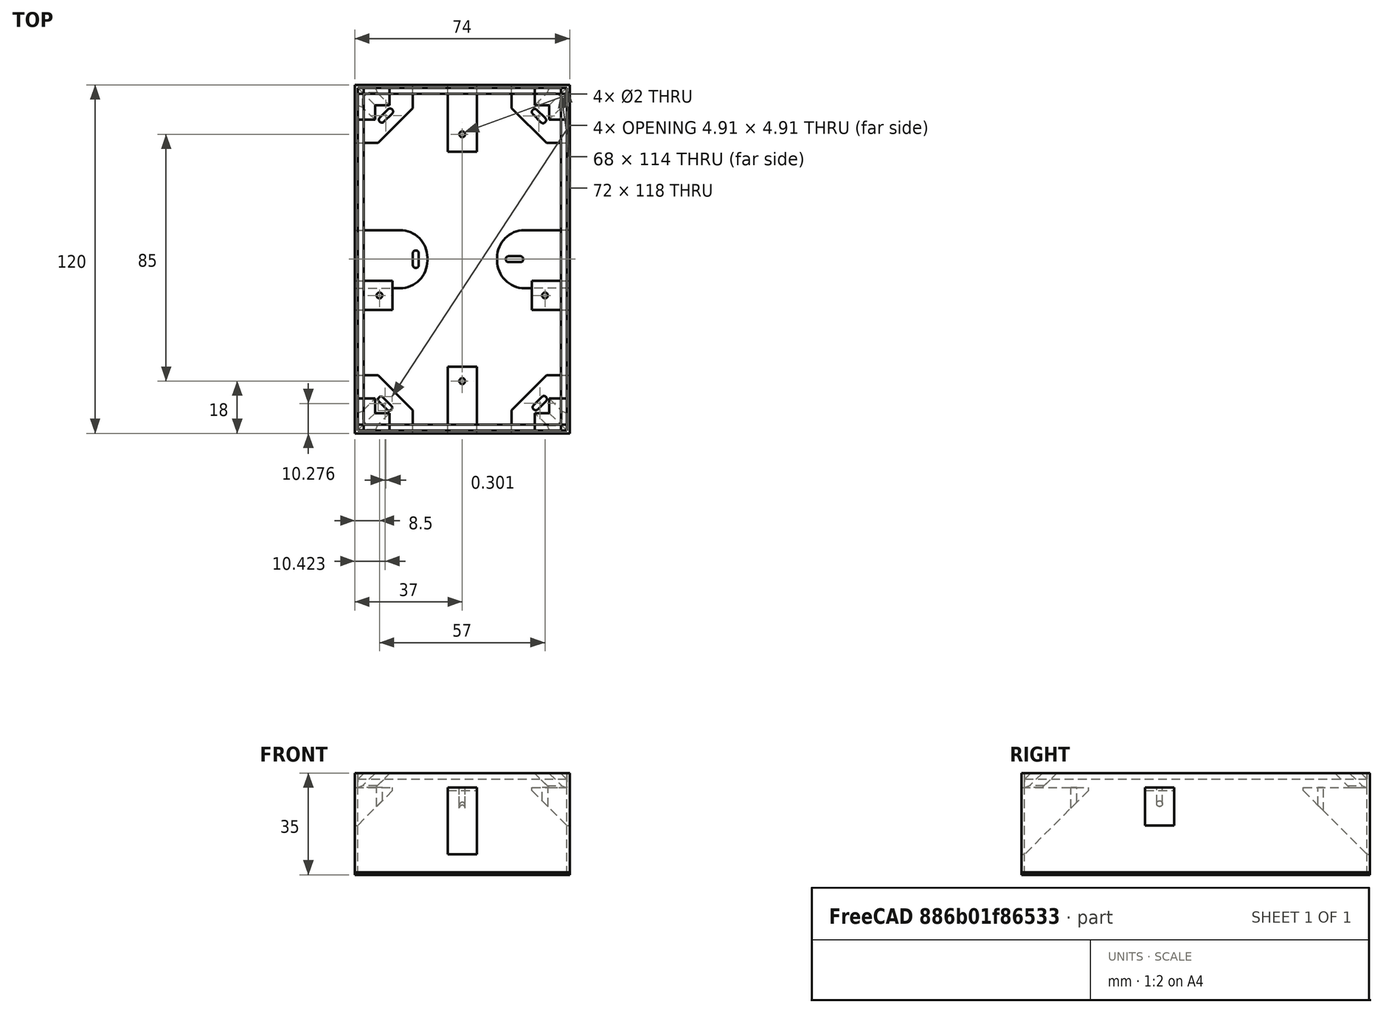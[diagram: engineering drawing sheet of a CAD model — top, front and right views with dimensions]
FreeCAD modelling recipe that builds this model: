
FCSTD DOCUMENT  (FreeCAD 0.16R)
Label: sonoff-T1-US-aufputz-v2-3
License: All rights reserved
LicenseURL: http://en.wikipedia.org/wiki/All_rights_reserved
objects: Part::Box×32, Part::Chamfer×20, Part::Cut×16, Part::Fillet×8, Part::Cylinder×4
note: 80 computed .brp shape members not serialized (recipe doc carries the construction recipe); baked Part::Feature solids carry a one-line shape summary decoded from their .brp

FEATURE [Part::Box] Box  label="Basis"
  Height = 35
  Length = 74
  Width = 120
FEATURE [Part::Box] Box001  label="Ausschnitt"
  Height = 35
  Length = 72
  Placement = pos=(1,1,0) rot=(0,0,1;0rad)
  Width = 118
FEATURE [Part::Cut] Cut
  Base = -> Box
  Tool = -> Box001
FEATURE [Part::Box] Box016  label="Cube012"
  Height = 0.8
  Length = 20
  Width = 20
FEATURE [Part::Box] Box017  label="Cube013"
  Height = 0.8
  Length = 20
  Placement = pos=(54,0,0) rot=(0,0,1;0rad)
  Width = 20
FEATURE [Part::Box] Box018  label="Cube014"
  Height = 0.8
  Length = 20
  Placement = pos=(54,100,0) rot=(0,0,1;0rad)
  Width = 20
FEATURE [Part::Box] Box019  label="Cube015"
  Height = 0.8
  Length = 20
  Placement = pos=(0,100,0) rot=(0,0,1;0rad)
  Width = 20
FEATURE [Part::Box] Box015  label="Basis002"
  Height = 0.8
  Length = 68
  Placement = pos=(3,3,0) rot=(0,0,1;0rad)
  Width = 114
FEATURE [Part::Box] Box014  label="Basis001"
  Height = 0.8
  Length = 74
  Width = 120
FEATURE [Part::Cut] Cut009
  Base = -> Box014
  Tool = -> Box015
FEATURE [Part::Chamfer] Chamfer
  Base = -> Box019
  Edges = 1 edges r=12: [Edge5]
FEATURE [Part::Chamfer] Chamfer001
  Base = -> Box018
  Edges = 1 edges r=12: [Edge1]
FEATURE [Part::Chamfer] Chamfer002
  Base = -> Box017
  Edges = 1 edges r=12: [Edge3]
FEATURE [Part::Chamfer] Chamfer003
  Base = -> Box016
  Edges = 1 edges r=12: [Edge7]
FEATURE [Part::Box] Box024  label="Cube019"
  Height = 5
  Length = 5
  Placement = pos=(63,109,30) rot=(0,0,1;0rad)
  Width = 5
FEATURE [Part::Box] Box025  label="Cube020"
  Height = 5
  Length = 11
  Placement = pos=(63,109,30) rot=(0,0,1;0rad)
  Width = 11
FEATURE [Part::Cut] Cut012
  Base = -> Box025
  Tool = -> Box024
FEATURE [Part::Chamfer] Chamfer004
  Base = -> Cut012
  Edges = 4 edges r=4.9: [Edge4,Edge5,Edge15,Edge16]
  Placement = pos=(-1,-1,0) rot=(0,0,1;0rad)
FEATURE [Part::Box] Box028  label="Cube023"
  Height = 2
  Length = 72
  Placement = pos=(1,1,33) rot=(0,0,1;0rad)
  Width = 2
FEATURE [Part::Box] Box029  label="Cube024"
  Height = 2
  Length = 2
  Placement = pos=(1,1,33) rot=(0,0,1;0rad)
  Width = 118
FEATURE [Part::Box] Box030  label="Cube025"
  Height = 2
  Length = 72
  Placement = pos=(1,117,33) rot=(0,0,1;0rad)
  Width = 2
FEATURE [Part::Box] Box031  label="Cube026"
  Height = 2
  Length = 2
  Placement = pos=(71,1,33) rot=(0,0,1;0rad)
  Width = 118
FEATURE [Part::Chamfer] Chamfer008
  Base = -> Box031
  Edges = 1 edges r=1.9: [Edge4]
FEATURE [Part::Chamfer] Chamfer009
  Base = -> Box030
  Edges = 1 edges r=1.9: [Edge9]
FEATURE [Part::Chamfer] Chamfer010
  Base = -> Box029
  Edges = 1 edges r=1.9: [Edge8]
FEATURE [Part::Chamfer] Chamfer011
  Base = -> Box028
  Edges = 1 edges r=1.9: [Edge11]
FEATURE [Part::Box] Box032  label="Cube027"
  Height = 5
  Length = 11
  Placement = pos=(63,109,30) rot=(0,0,1;0rad)
  Width = 11
FEATURE [Part::Box] Box033  label="Cube028"
  Height = 5
  Length = 5
  Placement = pos=(63,109,30) rot=(0,0,1;0rad)
  Width = 5
FEATURE [Part::Cut] Cut013
  Base = -> Box032
  Tool = -> Box033
FEATURE [Part::Chamfer] Chamfer012
  Base = -> Cut013
  Edges = 4 edges r=4.9: [Edge4,Edge5,Edge15,Edge16]
  Placement = pos=(121,45,0) rot=(0,0,1;1.5708rad)
FEATURE [Part::Chamfer] Chamfer013
  Base = -> Chamfer004
  Edges = 2 edges r=0.9: [Edge19,Edge23]
FEATURE [Part::Chamfer] Chamfer014
  Base = -> Chamfer012
  Edges = 2 edges r=0.9: [Edge19,Edge23]
FEATURE [Part::Box] Box034  label="Cube029"
  Height = 5
  Length = 5
  Placement = pos=(63,109,30) rot=(0,0,1;0rad)
  Width = 5
FEATURE [Part::Box] Box035  label="Cube030"
  Height = 5
  Length = 11
  Placement = pos=(63,109,30) rot=(0,0,1;0rad)
  Width = 11
FEATURE [Part::Cut] Cut014
  Base = -> Box035
  Tool = -> Box034
FEATURE [Part::Chamfer] Chamfer015
  Base = -> Cut014
  Edges = 4 edges r=4.9: [Edge4,Edge5,Edge15,Edge16]
  Placement = pos=(-1,-1,0) rot=(0,0,1;0rad)
FEATURE [Part::Chamfer] Chamfer016
  Base = -> Chamfer015
  Edges = 2 edges r=0.9: [Edge19,Edge23]
  Placement = pos=(74,120,0) rot=(0,0,1;3.14159rad)
FEATURE [Part::Box] Box036  label="Cube031"
  Height = 5
  Length = 5
  Placement = pos=(63,109,30) rot=(0,0,1;0rad)
  Width = 5
FEATURE [Part::Box] Box037  label="Cube032"
  Height = 5
  Length = 11
  Placement = pos=(63,109,30) rot=(0,0,1;0rad)
  Width = 11
FEATURE [Part::Cut] Cut015
  Base = -> Box037
  Tool = -> Box036
FEATURE [Part::Chamfer] Chamfer017
  Base = -> Cut015
  Edges = 4 edges r=4.9: [Edge4,Edge5,Edge15,Edge16]
  Placement = pos=(-1,-1,0) rot=(0,0,1;0rad)
FEATURE [Part::Chamfer] Chamfer018
  Base = -> Chamfer017
  Edges = 2 edges r=0.9: [Edge19,Edge23]
  Placement = pos=(-46,74,0) rot=(0,0,-1;1.5708rad)
FEATURE [Part::Box] Box038  label="Cube"
  Height = 13
  Length = 13
  Placement = pos=(0,42.5,17) rot=(0,0,1;0rad)
  Width = 10
FEATURE [Part::Box] Box039  label="Cube033"
  Height = 13
  Length = 13
  Placement = pos=(61,42.5,17) rot=(0,0,1;0rad)
  Width = 10
FEATURE [Part::Box] Box040  label="Cube034"
  Height = 23
  Length = 10
  Placement = pos=(32,0,7) rot=(0,0,1;0rad)
  Width = 23
FEATURE [Part::Box] Box041  label="Cube035"
  Height = 23
  Length = 10
  Placement = pos=(32,97,7) rot=(0,0,1;0rad)
  Width = 23
FEATURE [Part::Chamfer] Chamfer019
  Base = -> Box040
  Edges = 1 edges r=22: [Edge11]
FEATURE [Part::Chamfer] Chamfer020
  Base = -> Box041
  Edges = 1 edges r=22: [Edge9]
FEATURE [Part::Chamfer] Chamfer021
  Base = -> Box038
  Edges = 1 edges r=12: [Edge8]
FEATURE [Part::Chamfer] Chamfer022
  Base = -> Box039
  Edges = 1 edges r=12: [Edge4]
FEATURE [Part::Cylinder] Cylinder
  Angle = 360
  Height = 40
  Placement = pos=(37,18,0) rot=(0,0,1;0rad)
  Radius = 1
FEATURE [Part::Cylinder] Cylinder001
  Angle = 360
  Height = 40
  Placement = pos=(37,103,0) rot=(0,0,1;0rad)
  Radius = 1
FEATURE [Part::Cylinder] Cylinder002
  Angle = 360
  Height = 40
  Placement = pos=(8.5,47.5,0) rot=(0,0,1;0rad)
  Radius = 1
FEATURE [Part::Cylinder] Cylinder003
  Angle = 360
  Height = 40
  Placement = pos=(65.5,47.5,0) rot=(0,0,1;0rad)
  Radius = 1
FEATURE [Part::Cut] Cut016
  Base = -> Chamfer019
  Tool = -> Cylinder
FEATURE [Part::Cut] Cut017
  Base = -> Chamfer022
  Tool = -> Cylinder003
FEATURE [Part::Cut] Cut018
  Base = -> Chamfer021
  Tool = -> Cylinder002
FEATURE [Part::Cut] Cut019
  Base = -> Chamfer020
  Tool = -> Cylinder001
FEATURE [Part::Box] Box042  label="Cube036"
  Height = 0.8
  Length = 25
  Placement = pos=(0,50,0) rot=(0,0,1;0rad)
  Width = 20
FEATURE [Part::Fillet] Fillet
  Base = -> Box042
  Edges = 2 edges r=9.5: [Edge5,Edge7]
FEATURE [Part::Box] Box043  label="Cube037"
  Height = 10
  Length = 2
  Placement = pos=(20,57,0) rot=(0,0,1;0rad)
  Width = 6
FEATURE [Part::Box] Box044  label="Cube038"
  Height = 0.8
  Length = 25
  Placement = pos=(0,50,0) rot=(0,0,1;0rad)
  Width = 20
FEATURE [Part::Fillet] Fillet001
  Base = -> Box044
  Edges = 2 edges r=9.5: [Edge5,Edge7]
  Placement = pos=(74,120,0) rot=(0,0,1;3.14159rad)
FEATURE [Part::Box] Box045  label="Cube039"
  Height = 10
  Length = 6
  Placement = pos=(52,59,0) rot=(0,0,1;0rad)
  Width = 2
FEATURE [Part::Fillet] Fillet002
  Base = -> Box043
  Edges = 4 edges r=0.9: [Edge1,Edge3,Edge5,Edge7]
FEATURE [Part::Fillet] Fillet003
  Base = -> Box045
  Edges = 4 edges r=0.9: [Edge1,Edge3,Edge5,Edge7]
FEATURE [Part::Box] Box046  label="Cube040"
  Height = 10
  Length = 2
  Placement = pos=(20,57,0) rot=(0,0,1;0rad)
  Width = 6
FEATURE [Part::Fillet] Fillet004
  Base = -> Box046
  Edges = 4 edges r=0.9: [Edge1,Edge3,Edge5,Edge7]
  Placement = pos=(91,52,0) rot=(0,0,1;0.785398rad)
FEATURE [Part::Box] Box047  label="Cube041"
  Height = 10
  Length = 2
  Placement = pos=(20,57,0) rot=(0,0,1;0rad)
  Width = 6
FEATURE [Part::Fillet] Fillet005
  Base = -> Box047
  Edges = 4 edges r=0.9: [Edge1,Edge3,Edge5,Edge7]
  Placement = pos=(38,-47,0) rot=(0,0,1;0.785398rad)
FEATURE [Part::Box] Box048  label="Cube042"
  Height = 10
  Length = 2
  Placement = pos=(20,57,0) rot=(0,0,1;0rad)
  Width = 6
FEATURE [Part::Fillet] Fillet006
  Base = -> Box048
  Edges = 4 edges r=0.9: [Edge1,Edge3,Edge5,Edge7]
  Placement = pos=(121,38,0) rot=(0,0,1;2.35619rad)
FEATURE [Part::Box] Box049  label="Cube043"
  Height = 10
  Length = 2
  Placement = pos=(20,57,0) rot=(0,0,1;0rad)
  Width = 6
FEATURE [Part::Fillet] Fillet007
  Base = -> Box049
  Edges = 4 edges r=0.9: [Edge1,Edge3,Edge5,Edge7]
  Placement = pos=(68,137,0) rot=(0,0,1;2.35619rad)
FEATURE [Part::Cut] Cut020
  Base = -> Fillet
  Tool = -> Fillet002
FEATURE [Part::Cut] Cut021
  Base = -> Fillet001
  Tool = -> Fillet003
FEATURE [Part::Cut] Cut022
  Base = -> Chamfer
  Tool = -> Fillet007
FEATURE [Part::Cut] Cut023
  Base = -> Chamfer001
  Tool = -> Fillet004
FEATURE [Part::Cut] Cut024
  Base = -> Chamfer003
  Tool = -> Fillet005
FEATURE [Part::Cut] Cut025
  Base = -> Chamfer002
  Tool = -> Fillet006
